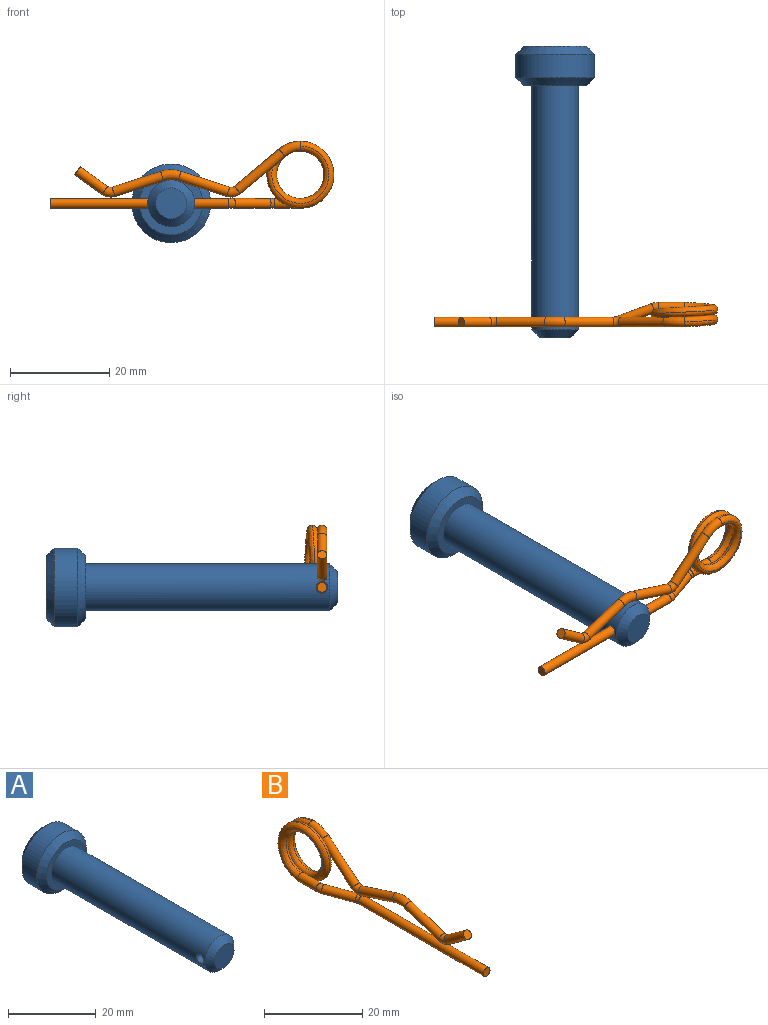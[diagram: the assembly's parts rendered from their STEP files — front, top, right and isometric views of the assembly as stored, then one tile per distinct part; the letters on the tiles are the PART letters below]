
ASSEMBLY  parts=2 mates=1
PART A: 9 faces, bbox 15.9x58.7x15.9 mm
  f0: cylinder r=4.71mm len=49.21mm, axis (0,1,0), area 1447.9mm2, adj f3,f5,f8
  f1: cylinder r=7.94mm len=15.88mm, axis (0,-1,0), area 237.5mm2, adj f6,f7
  f2: plane 12.7x12.7mm, normal (0,1,0), area 126.7mm2, adj f6
  f3: plane 12.7x12.7mm, normal (0,-1,0), area 56.9mm2, adj f0,f7
  f4: plane 6.25x6.25mm, normal (0,-1,0), area 30.7mm2, adj f8
  f5: cylinder r=1.19mm len=9.42mm, axis (-1,0,0), area 69.4mm2, adj f0
  f6: cone r=7.94mm half-angle=45deg, axis (0,-1,0), area 100.8mm2, adj f1,f2
  f7: cone r=6.35mm half-angle=45deg, axis (0,1,0), area 100.8mm2, adj f1,f3
  f8: cone r=3.12mm half-angle=45deg, axis (0,1,0), area 55.3mm2, adj f0,f4
PART B: 20 faces, bbox 5.2x57.5x14 mm
  f0: torus R=5.75mm, axis (-1,0,0), area 22.4mm2, adj f6,f7,f15,f16,f17,f18
  f1: torus R=1.98mm, axis (-1,0,0), area 12.4mm2, adj f6,f8
  f2: torus R=5.75mm, axis (1,0,0), area 22.3mm2, adj f8,f9
  f3: torus R=1.98mm, axis (-1,0,0), area 11.6mm2, adj f9,f10
  f4: torus R=2.98mm, axis (0,0,1), area 6.5mm2, adj f11,f12
  f5: torus R=2.98mm, axis (0,0,-1), area 6.5mm2, adj f12,f13
  f6: cylinder r=0.99mm len=10.25mm, axis (0,-0.77,-0.64), area 68.5mm2, adj f0,f1,f7,f17
  f7: cylinder r=0.99mm len=2.44mm, axis (0,-0.77,-0.64), area 0.6mm2, adj f0,f6,f18
  f8: cylinder r=0.99mm len=10.4mm, axis (0,-0.95,0.31), area 64.1mm2, adj f1,f2
  f9: cylinder r=0.99mm len=10.4mm, axis (0,-0.95,-0.31), area 64.1mm2, adj f2,f3
  f10: cylinder r=0.99mm len=6.66mm, axis (0,-0.81,0.58), area 42.2mm2, adj f3,f19
  f11: cylinder r=0.99mm len=35.95mm, axis (0,-1,0), area 224.1mm2, adj f4,f14
  f12: cylinder r=0.99mm len=7.87mm, axis (-0.34,0.94,0), area 47.7mm2, adj f4,f5
  f13: cylinder r=0.99mm len=5.23mm, axis (0,1,0), area 31.4mm2, adj f5,f15,f16,f17,f18
  f14: plane 1.98x1.98mm, normal (0,-1,0), area 3.1mm2, adj f11
  f15: bspline ~14.19x13.49mm, area 93mm2, adj f0,f13,f16,f17
  f16: bspline ~11.51x11.48mm, area 75.3mm2, adj f0,f13,f15,f18
  f17: bspline ~13.49x13.46mm, area 90mm2, adj f0,f6,f13,f15,f18
  f18: bspline ~12.1x11.51mm, area 73.7mm2, adj f0,f7,f13,f16,f17
  f19: plane 1.98x1.61mm, normal (0,-0.81,0.58), area 3.1mm2, adj f10
PLACE A at identity
PLACE B rot(axis=(0,0,-1),90deg) t=(-24.38,-47.63,0)mm
MATE fastened B.f11 <-> A.f5  axis (-1,0,0) through (-24.38,-47.63,0)mm
